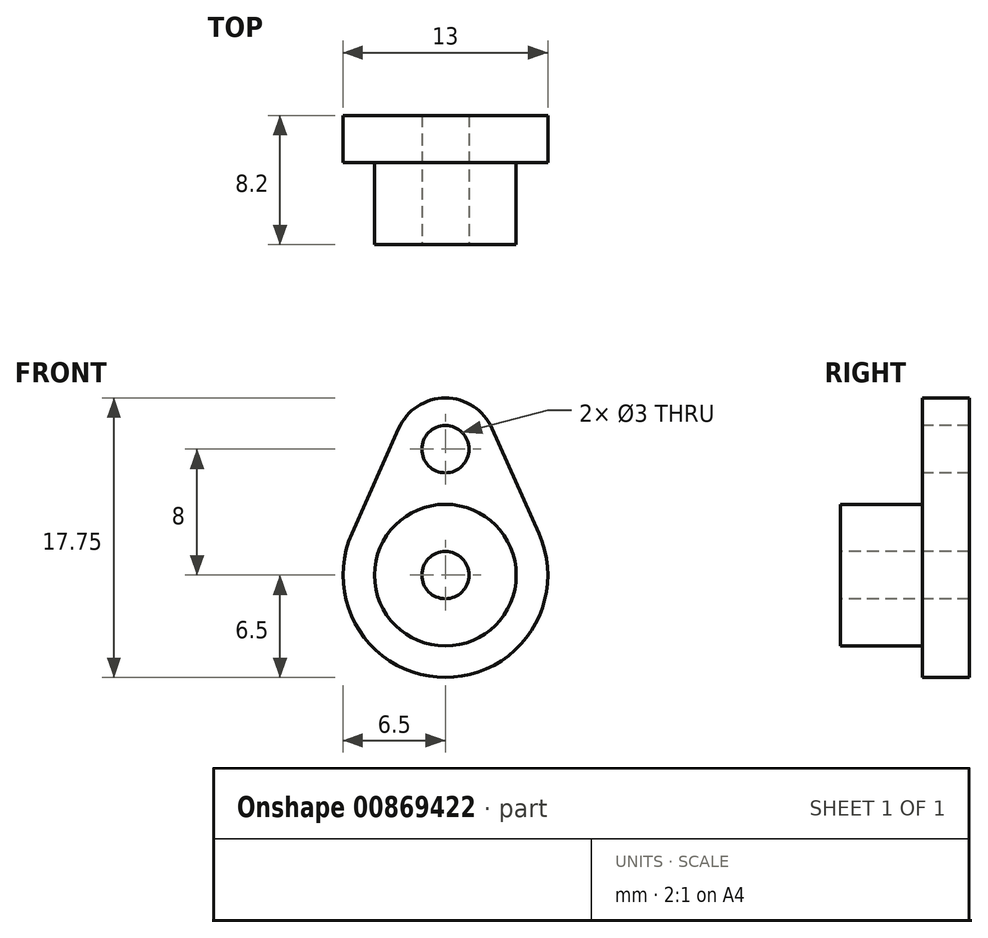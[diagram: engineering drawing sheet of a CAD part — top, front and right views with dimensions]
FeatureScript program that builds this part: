
annotation { "Feature Type Name" : "Feature", "Feature Type Description" : "" }
export const myFeature = defineFeature(function(context is Context, id is Id, definition is map)
    precondition{}
    {
        {
            var Q0;
            Q0=qCreatedBy(makeId("Front.planeOp"),FACE);
            var sketch = newSketch(context, id + "F0", { "sketchPlane" : qUnion([Q0])});
            skArc(sketch, "E0", {"start": v(2.97, 9.32) * mm, "mid": v(0, 11.25) * mm, "end": v(-2.97, 9.32) * mm});
            skCircle(sketch, "E1", {"center": v(0, 0) * mm, "radius": 1.5 * mm, "construction": true});
            skArc(sketch, "E2", {"start": v(-5.94, 2.64) * mm, "mid": v(0, -6.5) * mm, "end": v(5.94, 2.64) * mm});
            skLineSegment(sketch, "E3", {"start": v(-2.97, 9.32) * mm, "end": v(-5.94, 2.64) * mm});
            skLineSegment(sketch, "E4", {"start": v(2.97, 9.32) * mm, "end": v(5.94, 2.64) * mm});
            skCircle(sketch, "E5", {"center": v(0, 8) * mm, "radius": 1.5 * mm});
            skSolve(sketch);
        }
        {
            var Q0;
            Q0=makeQuery(id+"F0.imprint","IMPRINT",FACE,{"disambiguationData":[TD([[makeQuery(id+"F0.imprint","IMPRINT",EDGE,{"derivedFrom":sQuery(id+"F0.wireOp",EDGE,"E0")}),1.0]])]});
            extrude(context, id + "F1", {"entities" : qUnion([Q0]), "oppositeDirection" : true, "depth" : 3 * mm, "offsetDistance" : 25 * mm});
        }
        {
            var Q0;
            Q0=makeQuery(id+"F1.opExtrude","CAP_FACE",FACE,{"disambiguationData":[OSD([sQuery(id+"F0.wireOp",EDGE,"E0"),sQuery(id+"F0.wireOp",EDGE,"E2"),sQuery(id+"F0.wireOp",EDGE,"E3"),sQuery(id+"F0.wireOp",EDGE,"E4"),sQuery(id+"F0.wireOp",EDGE,"E5")])],"isStart":true});
            var sketch = newSketch(context, id + "F2", { "sketchPlane" : qUnion([Q0])});
            skCircle(sketch, "E6", {"center": v(0, 0) * mm, "radius": 4.5 * mm});
            skSolve(sketch);
        }
        {
            var Q0;
            Q0=makeQuery(id+"F2.imprint","IMPRINT",FACE,{"disambiguationData":[TD([[makeQuery(id+"F2.imprint","IMPRINT",EDGE,{"derivedFrom":sQuery(id+"F2.wireOp",EDGE,"E6")}),1.0]])]});
            extrude(context, id + "F3", {"entities" : qUnion([Q0]), "operationType" : NewBodyOperationType.ADD, "depth" : 5.2 * mm, "offsetDistance" : 25 * mm});
        }
        {
            var Q0;
            Q0=makeQuery(id+"F3.opExtrude","CAP_FACE",FACE,{"disambiguationData":[OSD([sQuery(id+"F2.wireOp",EDGE,"E6")])],"isStart":false});
            var sketch = newSketch(context, id + "F4", { "sketchPlane" : qUnion([Q0])});
            skCircle(sketch, "E7", {"center": v(0, 0) * mm, "radius": 1.5 * mm});
            skSolve(sketch);
        }
        {
            var Q0;
            Q0=makeQuery(id+"F4.imprint","IMPRINT",FACE,{"disambiguationData":[TD([[makeQuery(id+"F4.imprint","IMPRINT",EDGE,{"derivedFrom":sQuery(id+"F4.wireOp",EDGE,"E7")}),1.0]])]});
            extrude(context, id + "F5", {"entities" : qUnion([Q0]), "operationType" : NewBodyOperationType.REMOVE, "oppositeDirection" : true, "depth" : 20 * mm, "offsetDistance" : 25 * mm});
        }
    });
